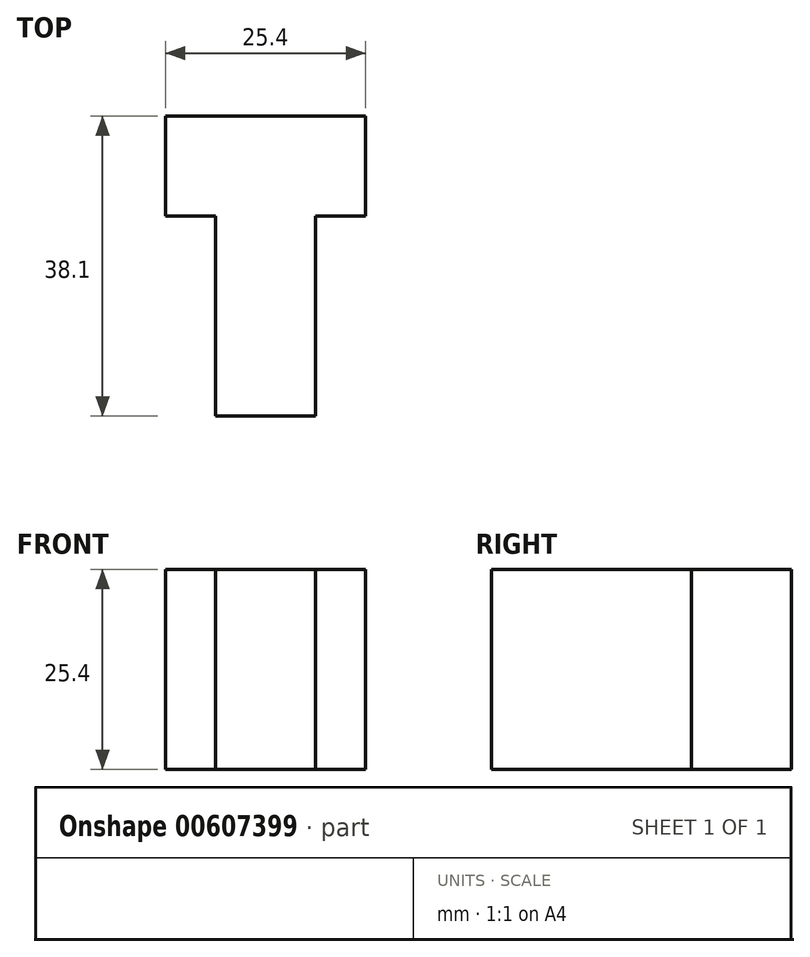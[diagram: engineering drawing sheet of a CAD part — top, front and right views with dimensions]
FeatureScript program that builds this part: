
annotation { "Feature Type Name" : "Feature", "Feature Type Description" : "" }
export const myFeature = defineFeature(function(context is Context, id is Id, definition is map)
    precondition{}
    {
        {
            var Q0;
            Q0=qCreatedBy(makeId("Top.planeOp"),FACE);
            var sketch = newSketch(context, id + "F0", { "sketchPlane" : qUnion([Q0])});
            skLineSegment(sketch, "E0", {"start": v(0, 0) * mm, "end": v(6.35, 0) * mm});
            skLineSegment(sketch, "E1", {"start": v(6.35, 0) * mm, "end": v(6.35, -25.4) * mm});
            skLineSegment(sketch, "E2", {"start": v(6.35, -25.4) * mm, "end": v(19.05, -25.4) * mm});
            skLineSegment(sketch, "E3", {"start": v(19.05, -25.4) * mm, "end": v(19.05, 0) * mm});
            skLineSegment(sketch, "E4", {"start": v(19.05, 0) * mm, "end": v(25.4, 0) * mm});
            skLineSegment(sketch, "E5", {"start": v(25.4, 0) * mm, "end": v(25.4, 12.7) * mm});
            skLineSegment(sketch, "E6", {"start": v(25.4, 12.7) * mm, "end": v(0, 12.7) * mm});
            skLineSegment(sketch, "E7", {"start": v(0, 12.7) * mm, "end": v(0, 0) * mm});
            skSolve(sketch);
        }
        {
            var Q0;
            Q0 = qSketchRegion(id + "F0", true);
            extrude(context, id + "F1", {"entities" : qUnion([Q0]), "depth" : 25.4 * mm, "offsetDistance" : 25.4 * mm});
        }
    });
